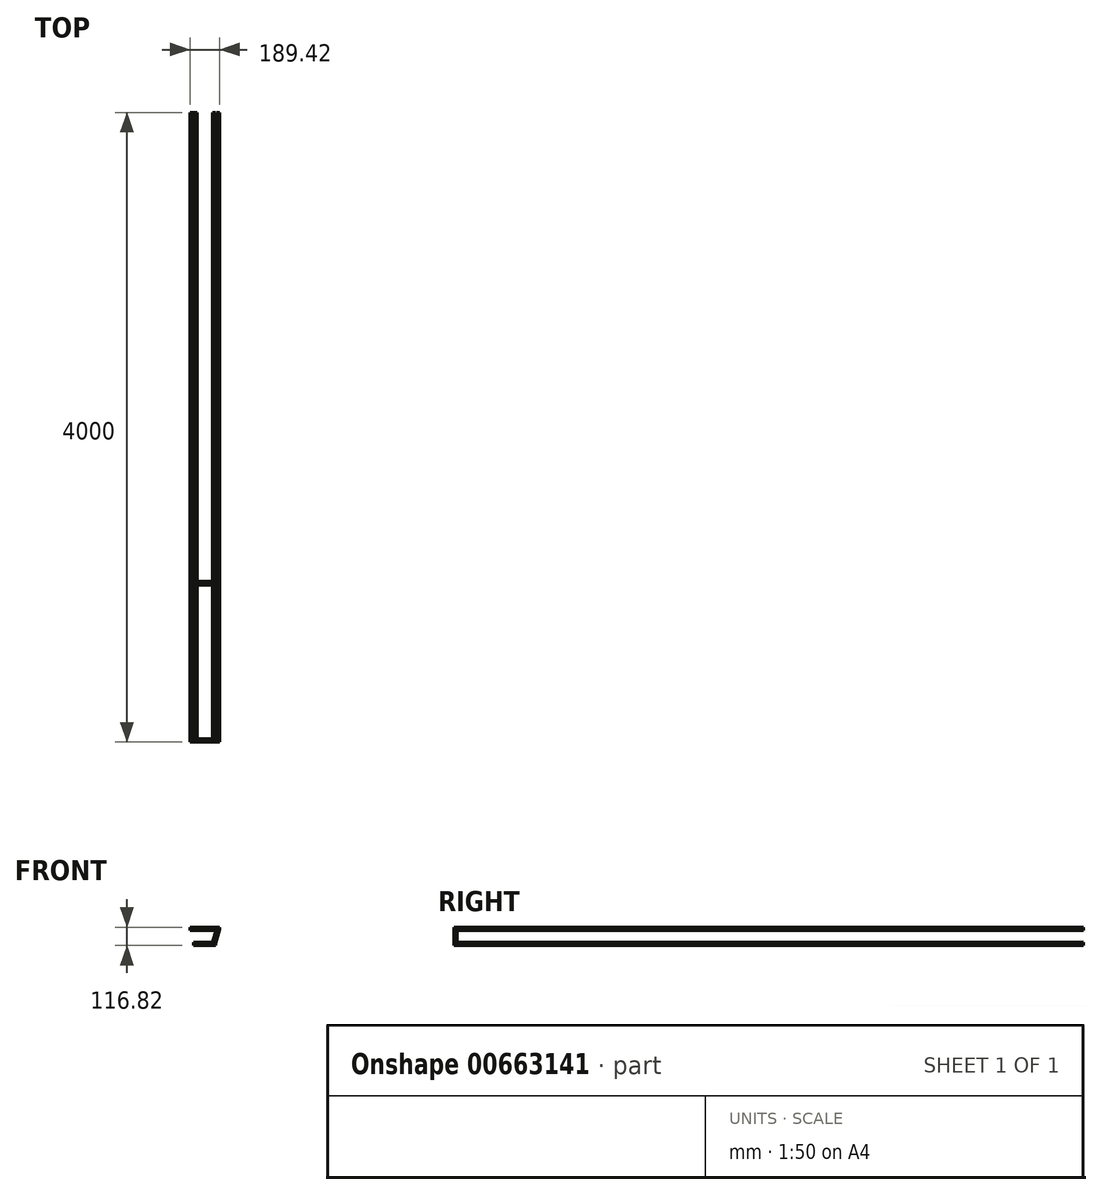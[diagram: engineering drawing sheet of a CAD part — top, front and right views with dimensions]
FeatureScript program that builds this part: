
annotation { "Feature Type Name" : "Feature", "Feature Type Description" : "" }
export const myFeature = defineFeature(function(context is Context, id is Id, definition is map)
    precondition{}
    {
        {
            var Q0;
            Q0=qCreatedBy(makeId("Front.planeOp"),FACE);
            var sketch = newSketch(context, id + "F0", { "sketchPlane" : qUnion([Q0])});
            skLineSegment(sketch, "E0.bottom", {"start": v(-94.6, 56.57) * mm, "end": v(-75.2, 56.57) * mm});
            skLineSegment(sketch, "E0.top", {"start": v(-94.6, 37.15) * mm, "end": v(-75.2, 37.15) * mm});
            skLineSegment(sketch, "E0.left", {"start": v(-94.6, 56.57) * mm, "end": v(-94.6, 37.15) * mm});
            skLineSegment(sketch, "E0.right", {"start": v(-75.2, 56.57) * mm, "end": v(-75.2, 37.15) * mm});
            skPoint(sketch, "E0.middle", {"position": v(-84.9, 46.86) * mm});
            skLineSegment(sketch, "E1.bottom", {"start": v(75.4, 56.57) * mm, "end": v(94.8, 56.57) * mm});
            skLineSegment(sketch, "E1.top", {"start": v(75.4, 37.15) * mm, "end": v(94.8, 37.15) * mm});
            skLineSegment(sketch, "E1.left", {"start": v(75.4, 56.57) * mm, "end": v(75.4, 37.15) * mm});
            skLineSegment(sketch, "E1.right", {"start": v(94.8, 56.57) * mm, "end": v(94.8, 37.15) * mm});
            skPoint(sketch, "E1.middle", {"position": v(85.1, 46.86) * mm});
            skLineSegment(sketch, "E2.bottom", {"start": v(50.4, -40.25) * mm, "end": v(69.8, -40.25) * mm});
            skLineSegment(sketch, "E2.top", {"start": v(50.4, -59.67) * mm, "end": v(69.8, -59.67) * mm});
            skLineSegment(sketch, "E2.left", {"start": v(50.4, -40.25) * mm, "end": v(50.4, -59.67) * mm});
            skLineSegment(sketch, "E2.right", {"start": v(69.8, -40.25) * mm, "end": v(69.8, -59.67) * mm});
            skPoint(sketch, "E2.middle", {"position": v(60.1, -49.96) * mm});
            skLineSegment(sketch, "E3.bottom", {"start": v(-69.6, -40.25) * mm, "end": v(-50.2, -40.25) * mm});
            skLineSegment(sketch, "E3.top", {"start": v(-69.6, -59.67) * mm, "end": v(-50.2, -59.67) * mm});
            skLineSegment(sketch, "E3.left", {"start": v(-69.6, -40.25) * mm, "end": v(-69.6, -59.67) * mm});
            skLineSegment(sketch, "E3.right", {"start": v(-50.2, -40.25) * mm, "end": v(-50.2, -59.67) * mm});
            skPoint(sketch, "E3.middle", {"position": v(-59.9, -49.96) * mm});
            skSolve(sketch);
        }
        {
            var Q0;
            Q0=qCreatedBy(makeId("Right.planeOp"),FACE);
            var sketch = newSketch(context, id + "F1", { "sketchPlane" : qUnion([Q0])});
            skLineSegment(sketch, "E4.bottom", {"start": v(0, 56.57) * mm, "end": v(20.13, 56.57) * mm});
            skLineSegment(sketch, "E4.top", {"start": v(0, 37.15) * mm, "end": v(20.13, 37.15) * mm});
            skLineSegment(sketch, "E4.left", {"start": v(0, 56.57) * mm, "end": v(0, 37.15) * mm});
            skLineSegment(sketch, "E4.right", {"start": v(20.13, 56.57) * mm, "end": v(20.13, 37.15) * mm});
            skLineSegment(sketch, "E5.bottom", {"start": v(0, -40.25) * mm, "end": v(20, -40.25) * mm});
            skLineSegment(sketch, "E5.top", {"start": v(0, -59.67) * mm, "end": v(20, -59.67) * mm});
            skLineSegment(sketch, "E5.left", {"start": v(0, -40.25) * mm, "end": v(0, -59.67) * mm});
            skLineSegment(sketch, "E5.right", {"start": v(20, -40.25) * mm, "end": v(20, -59.67) * mm});
            skLineSegment(sketch, "E6.bottom", {"start": v(999.25, 57.15) * mm, "end": v(1019.37, 57.15) * mm});
            skLineSegment(sketch, "E6.top", {"start": v(999.25, 37.15) * mm, "end": v(1019.37, 37.15) * mm});
            skLineSegment(sketch, "E6.left", {"start": v(999.25, 57.15) * mm, "end": v(999.25, 37.15) * mm});
            skLineSegment(sketch, "E6.right", {"start": v(1019.37, 57.15) * mm, "end": v(1019.37, 37.15) * mm});
            skLineSegment(sketch, "E7.bottom", {"start": v(1000.3, -39.67) * mm, "end": v(1020.43, -39.67) * mm});
            skLineSegment(sketch, "E7.top", {"start": v(1000.3, -59.67) * mm, "end": v(1020.43, -59.67) * mm});
            skLineSegment(sketch, "E7.left", {"start": v(1000.3, -39.67) * mm, "end": v(1000.3, -59.67) * mm});
            skLineSegment(sketch, "E7.right", {"start": v(1020.43, -39.67) * mm, "end": v(1020.43, -59.67) * mm});
            skSolve(sketch);
        }
        {
            var Q0;
            Q0=qCreatedBy(makeId("Top.planeOp"),FACE);
            var sketch = newSketch(context, id + "F2", { "sketchPlane" : qUnion([Q0])});
            skLineSegment(sketch, "E8.bottom", {"start": v(50.4, 0) * mm, "end": v(69.8, 0) * mm});
            skLineSegment(sketch, "E8.top", {"start": v(50.4, 20) * mm, "end": v(69.8, 20) * mm});
            skLineSegment(sketch, "E8.left", {"start": v(50.4, 0) * mm, "end": v(50.4, 20) * mm});
            skLineSegment(sketch, "E8.right", {"start": v(69.8, 0) * mm, "end": v(69.8, 20) * mm});
            skLineSegment(sketch, "E9.bottom", {"start": v(-69.6, 0) * mm, "end": v(-50.2, 0) * mm});
            skLineSegment(sketch, "E9.top", {"start": v(-69.6, 20) * mm, "end": v(-50.2, 20) * mm});
            skLineSegment(sketch, "E9.left", {"start": v(-69.6, 0) * mm, "end": v(-69.6, 20) * mm});
            skLineSegment(sketch, "E9.right", {"start": v(-50.2, 0) * mm, "end": v(-50.2, 20) * mm});
            skSolve(sketch);
        }
        {
            var Q0;
            Q0=makeQuery(id+"F0.imprint","IMPRINT",FACE,{"disambiguationData":[TD([[makeQuery(id+"F0.imprint","IMPRINT",EDGE,{"derivedFrom":sQuery(id+"F0.wireOp",EDGE,"E0.bottom")}),-1.0]])]});
            var Q1;
            Q1=makeQuery(id+"F0.imprint","IMPRINT",FACE,{"disambiguationData":[TD([[makeQuery(id+"F0.imprint","IMPRINT",EDGE,{"derivedFrom":sQuery(id+"F0.wireOp",EDGE,"E1.bottom")}),-1.0]])]});
            var Q2;
            Q2=makeQuery(id+"F0.imprint","IMPRINT",FACE,{"disambiguationData":[TD([[makeQuery(id+"F0.imprint","IMPRINT",EDGE,{"derivedFrom":sQuery(id+"F0.wireOp",EDGE,"E2.bottom")}),-1.0]])]});
            var Q3;
            Q3=makeQuery(id+"F0.imprint","IMPRINT",FACE,{"disambiguationData":[TD([[makeQuery(id+"F0.imprint","IMPRINT",EDGE,{"derivedFrom":sQuery(id+"F0.wireOp",EDGE,"E3.bottom")}),-1.0]])]});
            extrude(context, id + "F3", {"entities" : qUnion([Q0, Q1, Q2, Q3]), "oppositeDirection" : true, "depth" : 4000 * mm, "offsetDistance" : 25 * mm});
        }
        {
            var Q0;
            Q0=makeQuery(id+"F1.imprint","IMPRINT",FACE,{"disambiguationData":[TD([[makeQuery(id+"F1.imprint","IMPRINT",EDGE,{"derivedFrom":sQuery(id+"F1.wireOp",EDGE,"E4.bottom")}),-1.0]])]});
            extrude(context, id + "F4", {"entities" : qUnion([Q0]), "endBound" : BoundingType.SYMMETRIC, "depth" : 150 * mm, "offsetDistance" : 25 * mm});
        }
        {
            var Q0;
            Q0=makeQuery(id+"F1.imprint","IMPRINT",FACE,{"disambiguationData":[TD([[makeQuery(id+"F1.imprint","IMPRINT",EDGE,{"derivedFrom":sQuery(id+"F1.wireOp",EDGE,"E5.bottom")}),-1.0]])]});
            extrude(context, id + "F5", {"entities" : qUnion([Q0]), "endBound" : BoundingType.SYMMETRIC, "depth" : 100 * mm, "offsetDistance" : 25 * mm});
        }
        {
            var Q0;
            Q0=makeQuery(id+"F1.imprint","IMPRINT",FACE,{"disambiguationData":[TD([[makeQuery(id+"F1.imprint","IMPRINT",EDGE,{"derivedFrom":sQuery(id+"F1.wireOp",EDGE,"E6.bottom")}),-1.0]])]});
            extrude(context, id + "F6", {"entities" : qUnion([Q0]), "endBound" : BoundingType.SYMMETRIC, "depth" : 150 * mm, "offsetDistance" : 25 * mm});
        }
        {
            var Q0;
            Q0=makeQuery(id+"F1.imprint","IMPRINT",FACE,{"disambiguationData":[TD([[makeQuery(id+"F1.imprint","IMPRINT",EDGE,{"derivedFrom":sQuery(id+"F1.wireOp",EDGE,"E7.bottom")}),-1.0]])]});
            extrude(context, id + "F7", {"entities" : qUnion([Q0]), "endBound" : BoundingType.SYMMETRIC, "depth" : 100 * mm, "offsetDistance" : 25 * mm});
        }
        {
            var Q0;
            Q0=makeQuery(id+"F2.imprint","IMPRINT",FACE,{"disambiguationData":[TD([[makeQuery(id+"F2.imprint","IMPRINT",EDGE,{"derivedFrom":sQuery(id+"F2.wireOp",EDGE,"E8.bottom")}),1.0]])]});
            extrude(context, id + "F8", {"entities" : qUnion([Q0]), "endBound" : BoundingType.SYMMETRIC, "oppositeDirection" : true, "depth" : 90 * mm, "offsetDistance" : 25 * mm});
        }
        {
            var Q0;
            Q0=makeQuery(id+"F8.opExtrude","SWEPT_BODY",BODY,{"disambiguationData":[OSD([sQuery(id+"F2.wireOp",EDGE,"E8.bottom"),sQuery(id+"F2.wireOp",EDGE,"E8.top"),sQuery(id+"F2.wireOp",EDGE,"E8.left"),sQuery(id+"F2.wireOp",EDGE,"E8.right")])]});
            var Q1;
            Q1=makeQuery(id+"F8.opExtrude","CAP_EDGE",EDGE,{"disambiguationData":[OSD([sQuery(id+"F2.wireOp",EDGE,"E8.right")])],"isStart":false});
            transform(context, id + "F9", {"entities" : qUnion([Q0]), "transformType" : TransformType.ROTATION, "transformAxis" : qUnion([Q1]), "angle" : 16 * degree, "makeCopy" : false});
        }
    });
